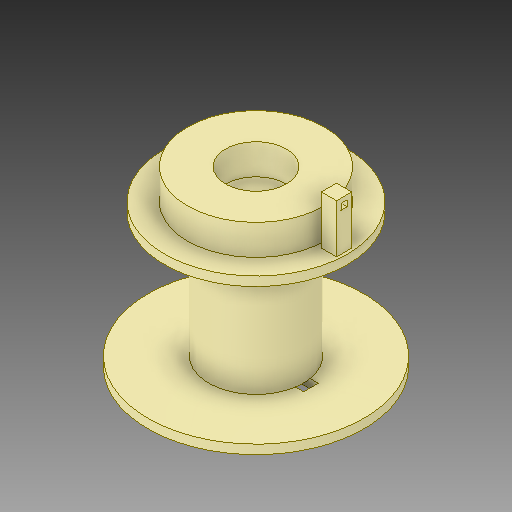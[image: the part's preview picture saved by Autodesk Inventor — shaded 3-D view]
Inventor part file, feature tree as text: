
AUTODESK INVENTOR PART (.ipt)
format: ipt  version: 2018 (Build 220112000, 112)  size: 445,952 bytes
history: native  units: mm
features: sketch x15, extrude x14, projected_geometry x2, pattern_circular x1, plane x1
ambient origin geometry x8: Origin, YZ Plane, XZ Plane, XY Plane, X Axis, Y Axis, Z Axis, Center Point
bodies: 实体1 (feature_tree)
feature tree (33):
  extrude  "拉伸1"  Depth=3.0mm TaperAngle=0.0deg
  extrude  "拉伸2"  Depth=25.0mm
  extrude  "拉伸3"  Depth=60.0mm
  extrude  "拉伸4"  Depth=3.0mm TaperAngle=0.0deg
  extrude  "拉伸5"  Depth=5.0mm TaperAngle=0.0deg
  extrude  "拉伸6"  Depth=45.0mm
  extrude  "拉伸7"  Depth=10.0mm
  extrude  "拉伸8"  Depth=3.0mm TaperAngle=0.0deg
  pattern_circular  "环形阵列1"  Count=2 Angle=360.0deg
  extrude  "拉伸9"  Depth=5.0mm
  extrude  "拉伸10"  Depth=5.0mm
  extrude  "拉伸11"  Depth=10.0mm
  extrude  "拉伸12"  Depth=13.5mm
  extrude  "拉伸13"  Depth=1.5mm
  plane  "工作平面2"
  sketch  "草图14"  dims[d40=13.0mm d41=13.5mm]
  extrude  "拉伸14"  Depth=17.5mm TaperAngle=0.0deg
  sketch  "草图1"  dims[d0=71.0mm d1=3.0mm d2=0.0mm]
  sketch  "草图2"  dims[d3=31.0mm d4=25.0mm]
  sketch  "草图3"  dims[d5=41.0mm d6=0.0mm d7=60.0mm]
  sketch  "草图4"  dims[d8=3.0mm d9=0.0mm d10=3.0mm d11=0.0mm]
  sketch  "草图5"  dims[d12=7.0mm d13=5.0mm d14=0.0mm]
  sketch  "草图6"  dims[d15=20.0mm d16=45.0mm]
  sketch  "草图7"  dims[d17=10.0mm d18=0.0mm d19=45.0mm]
  sketch  "草图8"  dims[d20=7.0mm d21=3.0mm d22=0.0mm]
  sketch  "草图9"  dims[d23=5.0mm]
  sketch  "草图10"  dims[d24=3.0mm d25=0.0mm d26=20.0mm d27=360.0deg]
  sketch  "草图11"  dims[d30=16.0mm d31=0.0mm d32=5.0mm]
  projected_geometry  "投影回路1"
  sketch  "草图12"  dims[d33=5.0mm d34=24.0mm]
  sketch  "草图13"  dims[d36=10.0mm d38=22.0mm]
  projected_geometry  "投影回路2"
  sketch  "草图15"  dims[d42=4.0mm d43=0.0mm d44=1.5mm d45=17.5mm d46=0.0mm d47=2.0mm d48=2.0mm d49=0.0mm d50=3.0mm d51=0.0mm d52=9.0mm d53=9.0mm d56=1.0mm d57=-1.0mm d58=1.0mm d59=10.0mm d60=0.0mm]
